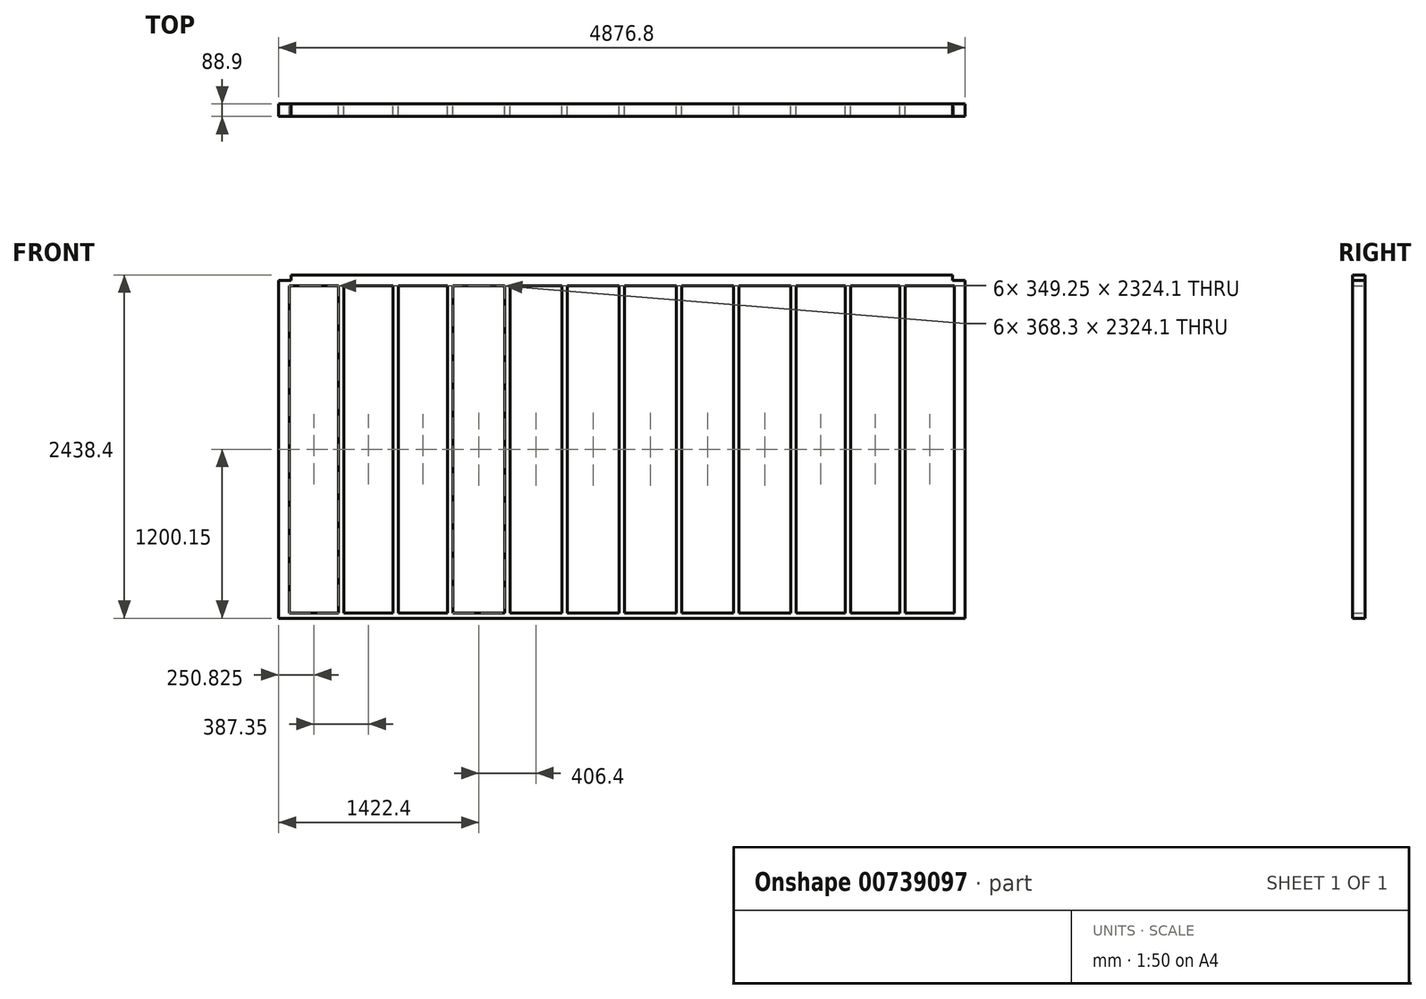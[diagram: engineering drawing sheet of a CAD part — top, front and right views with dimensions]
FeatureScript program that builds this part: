
annotation { "Feature Type Name" : "Feature", "Feature Type Description" : "" }
export const myFeature = defineFeature(function(context is Context, id is Id, definition is map)
    precondition{}
    {
        {
            var Q0;
            Q0=qCreatedBy(makeId("Front.planeOp"),FACE);
            var sketch = newSketch(context, id + "F0", { "sketchPlane" : qUnion([Q0])});
            skLineSegment(sketch, "E0.bottom", {"start": v(0, 0) * mm, "end": v(4876.8, 0) * mm});
            skLineSegment(sketch, "E0.top", {"start": v(0, 2400.3) * mm, "end": v(4876.8, 2400.3) * mm});
            skLineSegment(sketch, "E0.left", {"start": v(0, 0) * mm, "end": v(0, 2400.3) * mm});
            skLineSegment(sketch, "E0.right", {"start": v(4876.8, 0) * mm, "end": v(4876.8, 2400.3) * mm});
            skLineSegment(sketch, "E1.0", {"start": v(0, 38.1) * mm, "end": v(4876.8, 38.1) * mm});
            skLineSegment(sketch, "E2.0", {"start": v(0, 2362.2) * mm, "end": v(4876.8, 2362.2) * mm});
            skLineSegment(sketch, "E3", {"start": v(38.1, 2362.2) * mm, "end": v(38.1, 38.1) * mm});
            skLineSegment(sketch, "E4.0", {"start": v(76.2, 2362.2) * mm, "end": v(76.2, 38.1) * mm});
            skLineSegment(sketch, "E5", {"start": v(4838.7, 2362.2) * mm, "end": v(4838.7, 38.1) * mm});
            skLineSegment(sketch, "E6.0", {"start": v(4800.6, 2362.2) * mm, "end": v(4800.6, 38.1) * mm});
            skLineSegment(sketch, "E7", {"start": v(425.45, 2362.2) * mm, "end": v(425.45, 38.1) * mm});
            skLineSegment(sketch, "E8.0", {"start": v(463.55, 2362.2) * mm, "end": v(463.55, 38.1) * mm});
            skLineSegment(sketch, "E9", {"start": v(2012.95, 2362.2) * mm, "end": v(2012.95, 38.1) * mm});
            skLineSegment(sketch, "E10.0", {"start": v(2051.05, 2362.2) * mm, "end": v(2051.05, 38.1) * mm});
            skLineSegment(sketch, "E11", {"start": v(2438.4, 2362.2) * mm, "end": v(2438.4, -1355.37) * mm, "construction": true});
            skLineSegment(sketch, "E12", {"start": v(88.9, 2400.3) * mm, "end": v(88.9, 2438.4) * mm});
            skLineSegment(sketch, "E13", {"start": v(88.9, 2438.4) * mm, "end": v(4787.9, 2438.4) * mm});
            skLineSegment(sketch, "E14", {"start": v(4787.9, 2438.4) * mm, "end": v(4787.9, 2400.3) * mm});
            skLineSegment(sketch, "E15", {"start": v(812.8, 2362.2) * mm, "end": v(812.8, 38.1) * mm});
            skLineSegment(sketch, "E16", {"start": v(850.9, 2362.2) * mm, "end": v(850.9, 38.1) * mm});
            skLineSegment(sketch, "E17", {"start": v(1200.15, 2362.2) * mm, "end": v(1200.15, 38.1) * mm});
            skLineSegment(sketch, "E18", {"start": v(1238.25, 2362.2) * mm, "end": v(1238.25, 38.1) * mm});
            skLineSegment(sketch, "E19", {"start": v(1606.55, 2362.2) * mm, "end": v(1606.55, 38.1) * mm});
            skLineSegment(sketch, "E20", {"start": v(1644.65, 2362.2) * mm, "end": v(1644.65, 38.1) * mm});
            skLineSegment(sketch, "E21", {"start": v(1219.2, 2667.98) * mm, "end": v(1219.2, -391.72) * mm, "construction": true});
            skLineSegment(sketch, "E22", {"start": v(2419.35, 2362.2) * mm, "end": v(2419.35, 38.1) * mm});
            skLineSegment(sketch, "E23.MirrorCS", {"start": v(2457.45, 2362.2) * mm, "end": v(2457.45, 38.1) * mm});
            skLineSegment(sketch, "E24.MirrorCS", {"start": v(3270.25, 2362.2) * mm, "end": v(3270.25, 38.1) * mm});
            skLineSegment(sketch, "E25.MirrorCS", {"start": v(4064, 2362.2) * mm, "end": v(4064, 38.1) * mm});
            skLineSegment(sketch, "E26.MirrorCS", {"start": v(3676.65, 2362.2) * mm, "end": v(3676.65, 38.1) * mm});
            skLineSegment(sketch, "E27.MirrorCS", {"start": v(4413.25, 2362.2) * mm, "end": v(4413.25, 38.1) * mm});
            skLineSegment(sketch, "E28.MirrorCS", {"start": v(4451.35, 2362.2) * mm, "end": v(4451.35, 38.1) * mm});
            skLineSegment(sketch, "E29.MirrorCS", {"start": v(2825.75, 2362.2) * mm, "end": v(2825.75, 38.1) * mm});
            skLineSegment(sketch, "E30.MirrorCS", {"start": v(4025.9, 2362.2) * mm, "end": v(4025.9, 38.1) * mm});
            skLineSegment(sketch, "E31.MirrorCS", {"start": v(2863.85, 2362.2) * mm, "end": v(2863.85, 38.1) * mm});
            skLineSegment(sketch, "E32.MirrorCS", {"start": v(3638.55, 2362.2) * mm, "end": v(3638.55, 38.1) * mm});
            skLineSegment(sketch, "E33.MirrorCS", {"start": v(3232.15, 2362.2) * mm, "end": v(3232.15, 38.1) * mm});
            skLineSegment(sketch, "E34.MirrorCS", {"start": v(3657.6, 2667.98) * mm, "end": v(3657.6, -391.72) * mm, "construction": true});
            skSolve(sketch);
        }
        {
            var Q0;
            {var subQ5=sQuery(id+"F0.wireOp",EDGE,"E3");Q0=makeQuery(id+"F0.imprint","IMPRINT",FACE,{"disambiguationData":[TD([[makeQuery(id+"F0.imprint","IMPRINT",EDGE,{"derivedFrom":subQ5}),-1.0]])]});}
            var Q1;
            {var subQ0=sQuery(id+"F0.wireOp",EDGE,"E3");Q1=makeQuery(id+"F0.imprint","IMPRINT",FACE,{"disambiguationData":[TD([[makeQuery(id+"F0.imprint","IMPRINT",EDGE,{"derivedFrom":subQ0}),1.0]])]});}
            var Q2;
            {var subQ0=sQuery(id+"F0.wireOp",EDGE,"E7");Q2=makeQuery(id+"F0.imprint","IMPRINT",FACE,{"disambiguationData":[TD([[makeQuery(id+"F0.imprint","IMPRINT",EDGE,{"derivedFrom":subQ0}),1.0]])]});}
            var Q3;
            {var subQ0=sQuery(id+"F0.wireOp",EDGE,"E15");Q3=makeQuery(id+"F0.imprint","IMPRINT",FACE,{"disambiguationData":[TD([[makeQuery(id+"F0.imprint","IMPRINT",EDGE,{"derivedFrom":subQ0}),1.0]])]});}
            var Q4;
            {var subQ0=sQuery(id+"F0.wireOp",EDGE,"E17");Q4=makeQuery(id+"F0.imprint","IMPRINT",FACE,{"disambiguationData":[TD([[makeQuery(id+"F0.imprint","IMPRINT",EDGE,{"derivedFrom":subQ0}),1.0]])]});}
            var Q5;
            {var subQ0=sQuery(id+"F0.wireOp",EDGE,"E9");Q5=makeQuery(id+"F0.imprint","IMPRINT",FACE,{"disambiguationData":[TD([[makeQuery(id+"F0.imprint","IMPRINT",EDGE,{"derivedFrom":subQ0}),1.0]])]});}
            var Q6;
            {var subQ5=sQuery(id+"F0.wireOp",EDGE,"f1f4cbda-b9e4-48b1-9a52-18e84121c432.0");Q6=makeQuery(id+"F0.imprint","IMPRINT",FACE,{"disambiguationData":[TD([[makeQuery(id+"F0.imprint","IMPRINT",EDGE,{"derivedFrom":subQ5}),-1.0]])]});}
            var Q7;
            {var subQ5=sQuery(id+"F0.wireOp",EDGE,"09067e87-3c13-443e-8f31-6db11c8dc576.0");Q7=makeQuery(id+"F0.imprint","IMPRINT",FACE,{"disambiguationData":[TD([[makeQuery(id+"F0.imprint","IMPRINT",EDGE,{"derivedFrom":subQ5}),-1.0]])]});}
            var Q8;
            {var subQ5=sQuery(id+"F0.wireOp",EDGE,"Xp0Nxnc9-JDQc-rOWq-xaf3-x7MAriFLtKY5");Q8=makeQuery(id+"F0.imprint","IMPRINT",FACE,{"disambiguationData":[TD([[makeQuery(id+"F0.imprint","IMPRINT",EDGE,{"derivedFrom":subQ5}),1.0]])]});}
            var Q9;
            {var subQ5=sQuery(id+"F0.wireOp",EDGE,"uVg0DG5J-9Kwi-cZtZ-OEbZ-1IFQbZz8wRyh");Q9=makeQuery(id+"F0.imprint","IMPRINT",FACE,{"disambiguationData":[TD([[makeQuery(id+"F0.imprint","IMPRINT",EDGE,{"derivedFrom":subQ5}),-1.0]])]});}
            var Q10;
            {var subQ7=sQuery(id+"F0.wireOp",EDGE,"e65ddaba-fa81-4db5-b6f7-81f66d658137.0");Q10=makeQuery(id+"F0.imprint","IMPRINT",FACE,{"disambiguationData":[TD([[makeQuery(id+"F0.imprint","IMPRINT",EDGE,{"derivedFrom":subQ7}),1.0]])]});}
            var Q11;
            {var subQ0=sQuery(id+"F0.wireOp",EDGE,"1f1a9d3a-20b5-49f1-988e-2228e01d584c0.MirrorCS");Q11=makeQuery(id+"F0.imprint","IMPRINT",FACE,{"disambiguationData":[TD([[makeQuery(id+"F0.imprint","IMPRINT",EDGE,{"derivedFrom":subQ0}),1.0]])]});}
            var Q12;
            {var subQ0=sQuery(id+"F0.wireOp",EDGE,"1f1a9d3a-20b5-49f1-988e-2228e01d584c1.MirrorCS");Q12=makeQuery(id+"F0.imprint","IMPRINT",FACE,{"disambiguationData":[TD([[makeQuery(id+"F0.imprint","IMPRINT",EDGE,{"derivedFrom":subQ0}),1.0]])]});}
            var Q13;
            {var subQ0=sQuery(id+"F0.wireOp",EDGE,"1f1a9d3a-20b5-49f1-988e-2228e01d584c2.MirrorCS");Q13=makeQuery(id+"F0.imprint","IMPRINT",FACE,{"disambiguationData":[TD([[makeQuery(id+"F0.imprint","IMPRINT",EDGE,{"derivedFrom":subQ0}),1.0]])]});}
            var Q14;
            {var subQ0=sQuery(id+"F0.wireOp",EDGE,"E5");Q14=makeQuery(id+"F0.imprint","IMPRINT",FACE,{"disambiguationData":[TD([[makeQuery(id+"F0.imprint","IMPRINT",EDGE,{"derivedFrom":subQ0}),-1.0]])]});}
            var Q15;
            {var subQ5=sQuery(id+"F0.wireOp",EDGE,"E5");Q15=makeQuery(id+"F0.imprint","IMPRINT",FACE,{"disambiguationData":[TD([[makeQuery(id+"F0.imprint","IMPRINT",EDGE,{"derivedFrom":subQ5}),1.0]])]});}
            var Q16;
            {var subQ14=sQuery(id+"F0.wireOp",EDGE,"E0.top");var subQ22=sQuery(id+"F0.wireOp",EDGE,"E0.left");var subQ23=makeQuery(id+"F0.imprint","INTERSECT",VERTEX,{"derivedFrom":[subQ14,subQ22]});Q16=makeQuery(id+"F0.imprint","IMPRINT",FACE,{"disambiguationData":[TD([[makeQuery(id+"F0.imprint","IMPRINT",EDGE,{"disambiguationData":[TD([[subQ23,-1.0]])],"derivedFrom":subQ14}),-1.0]])]});}
            var Q17;
            {var subQ0=sQuery(id+"F0.wireOp",EDGE,"E12");Q17=makeQuery(id+"F0.imprint","IMPRINT",FACE,{"disambiguationData":[TD([[makeQuery(id+"F0.imprint","IMPRINT",EDGE,{"derivedFrom":subQ0}),-1.0]])]});}
            var Q18;
            {var subQ15=sQuery(id+"F0.wireOp",EDGE,"E0.bottom");Q18=makeQuery(id+"F0.imprint","IMPRINT",FACE,{"disambiguationData":[TD([[makeQuery(id+"F0.imprint","IMPRINT",EDGE,{"derivedFrom":subQ15}),1.0]])]});}
            var Q19;
            {var subQ0=sQuery(id+"F0.wireOp",EDGE,"E19");Q19=makeQuery(id+"F0.imprint","IMPRINT",FACE,{"disambiguationData":[TD([[makeQuery(id+"F0.imprint","IMPRINT",EDGE,{"derivedFrom":subQ0}),1.0]])]});}
            var Q20;
            {var subQ0=sQuery(id+"F0.wireOp",EDGE,"2aa97d75-183e-436c-b0b5-5b1d4690e7840.MirrorCS");Q20=makeQuery(id+"F0.imprint","IMPRINT",FACE,{"disambiguationData":[TD([[makeQuery(id+"F0.imprint","IMPRINT",EDGE,{"derivedFrom":subQ0}),-1.0]])]});}
            var Q21;
            {var subQ0=sQuery(id+"F0.wireOp",EDGE,"E22");Q21=makeQuery(id+"F0.imprint","IMPRINT",FACE,{"disambiguationData":[TD([[makeQuery(id+"F0.imprint","IMPRINT",EDGE,{"derivedFrom":subQ0}),1.0]])]});}
            var Q22;
            {var subQ0=sQuery(id+"F0.wireOp",EDGE,"E29.MirrorCS");Q22=makeQuery(id+"F0.imprint","IMPRINT",FACE,{"disambiguationData":[TD([[makeQuery(id+"F0.imprint","IMPRINT",EDGE,{"derivedFrom":subQ0}),1.0]])]});}
            var Q23;
            {var subQ0=sQuery(id+"F0.wireOp",EDGE,"E24.MirrorCS");Q23=makeQuery(id+"F0.imprint","IMPRINT",FACE,{"disambiguationData":[TD([[makeQuery(id+"F0.imprint","IMPRINT",EDGE,{"derivedFrom":subQ0}),-1.0]])]});}
            var Q24;
            {var subQ0=sQuery(id+"F0.wireOp",EDGE,"E26.MirrorCS");Q24=makeQuery(id+"F0.imprint","IMPRINT",FACE,{"disambiguationData":[TD([[makeQuery(id+"F0.imprint","IMPRINT",EDGE,{"derivedFrom":subQ0}),-1.0]])]});}
            var Q25;
            {var subQ0=sQuery(id+"F0.wireOp",EDGE,"E25.MirrorCS");Q25=makeQuery(id+"F0.imprint","IMPRINT",FACE,{"disambiguationData":[TD([[makeQuery(id+"F0.imprint","IMPRINT",EDGE,{"derivedFrom":subQ0}),-1.0]])]});}
            var Q26;
            {var subQ0=sQuery(id+"F0.wireOp",EDGE,"E27.MirrorCS");Q26=makeQuery(id+"F0.imprint","IMPRINT",FACE,{"disambiguationData":[TD([[makeQuery(id+"F0.imprint","IMPRINT",EDGE,{"derivedFrom":subQ0}),1.0]])]});}
            extrude(context, id + "F1", {"entities" : qUnion([Q0, Q1, Q2, Q3, Q4, Q5, Q6, Q7, Q8, Q9, Q10, Q11, Q12, Q13, Q14, Q15, Q16, Q17, Q18, Q19, Q20, Q21, Q22, Q23, Q24, Q25, Q26]), "depth" : 88.9 * mm, "offsetDistance" : 25.4 * mm});
        }
    });
